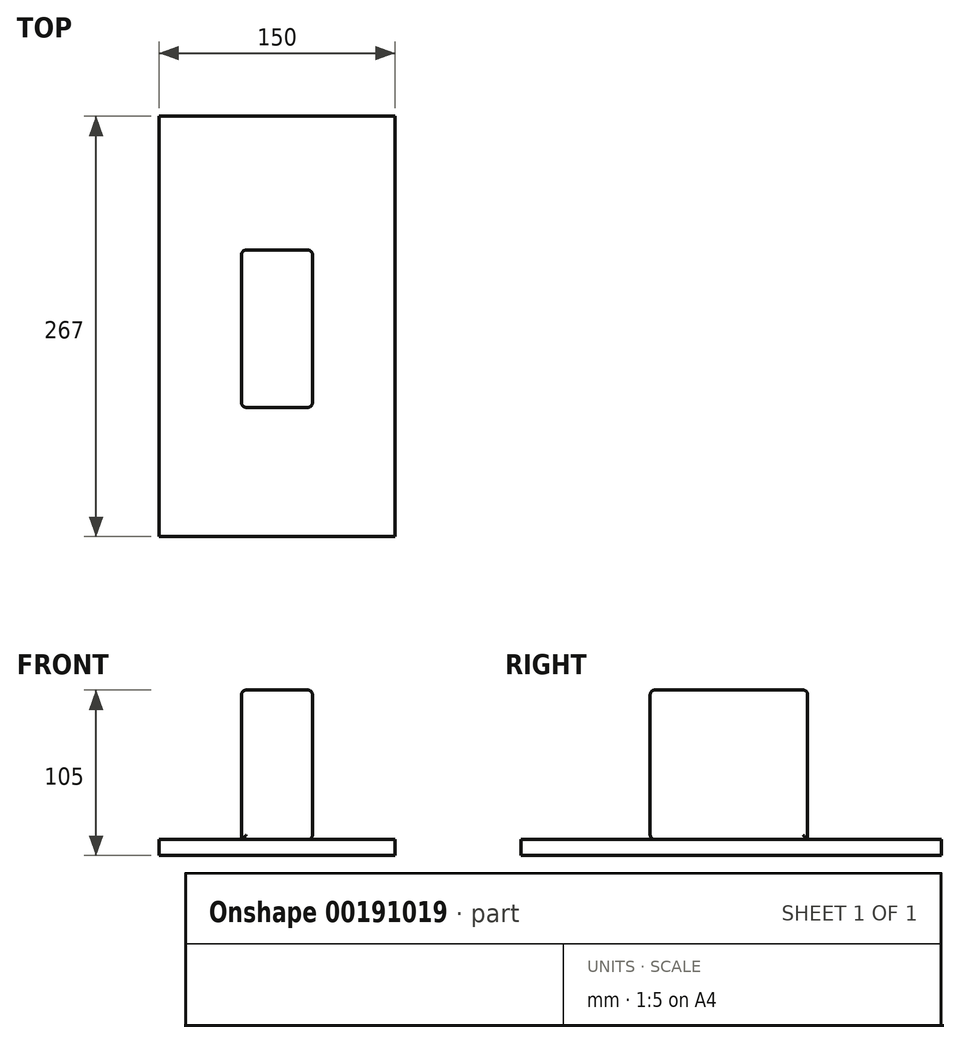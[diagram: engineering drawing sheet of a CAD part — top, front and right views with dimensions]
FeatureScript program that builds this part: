
annotation { "Feature Type Name" : "Feature", "Feature Type Description" : "" }
export const myFeature = defineFeature(function(context is Context, id is Id, definition is map)
    precondition{}
    {
        {
            var Q0;
            Q0=qCreatedBy(makeId("Front.planeOp"),FACE);
            var sketch = newSketch(context, id + "F0", { "sketchPlane" : qUnion([Q0])});
            skLineSegment(sketch, "E0.bottom", {"start": v(-22.5, -47.5) * mm, "end": v(22.5, -47.5) * mm});
            skLineSegment(sketch, "E0.top", {"start": v(-22.5, 47.5) * mm, "end": v(22.5, 47.5) * mm});
            skLineSegment(sketch, "E0.left", {"start": v(-22.5, -47.5) * mm, "end": v(-22.5, 47.5) * mm});
            skLineSegment(sketch, "E0.right", {"start": v(22.5, -47.5) * mm, "end": v(22.5, 47.5) * mm});
            skPoint(sketch, "E0.middle", {"position": v(0, 0) * mm});
            skSolve(sketch);
        }
        {
            var Q0;
            Q0 = qSketchRegion(id + "F0", true);
            extrude(context, id + "F1", {"entities" : qUnion([Q0]), "depth" : 100 * mm});
        }
        {
            var Q0;
            Q0=makeQuery(id+"F1.opExtrude","CAP_EDGE",EDGE,{"disambiguationData":[OSD([sQuery(id+"F0.wireOp",EDGE,"E0.right")])],"isStart":false});
            var Q1;
            Q1=makeQuery(id+"F1.opExtrude","CAP_FACE",FACE,{"disambiguationData":[OSD([sQuery(id+"F0.wireOp",EDGE,"E0.bottom"),sQuery(id+"F0.wireOp",EDGE,"E0.top"),sQuery(id+"F0.wireOp",EDGE,"E0.left"),sQuery(id+"F0.wireOp",EDGE,"E0.right")])],"isStart":false});
            var Q2;
            Q2=makeQuery(id+"F1.opExtrude","CAP_EDGE",EDGE,{"disambiguationData":[OSD([sQuery(id+"F0.wireOp",EDGE,"E0.right")])],"isStart":true});
            var Q3;
            Q3=makeQuery(id+"F1.opExtrude","CAP_EDGE",EDGE,{"disambiguationData":[OSD([sQuery(id+"F0.wireOp",EDGE,"E0.left")])],"isStart":true});
            var Q4;
            Q4=makeQuery(id+"F1.opExtrude","SWEPT_FACE",FACE,{"disambiguationData":[OSD([sQuery(id+"F0.wireOp",EDGE,"E0.right")])]});
            var Q5;
            Q5=makeQuery(id+"F1.opExtrude","SWEPT_EDGE",EDGE,{"disambiguationData":[OSD([sQuery(id+"F0.wireOp",EDGE,"E0.top"),sQuery(id+"F0.wireOp",EDGE,"E0.left")])]});
            var Q6;
            Q6=makeQuery(id+"F1.opExtrude","CAP_EDGE",EDGE,{"disambiguationData":[OSD([sQuery(id+"F0.wireOp",EDGE,"E0.top")])],"isStart":true});
            fillet(context, id + "F2", {"entities" : qUnion([Q0, Q1, Q2, Q3, Q4, Q5, Q6]), "radius" : 3 * mm, "tangentPropagation" : true, "allowEdgeOverflow" : false});
        }
        {
            var Q0;
            Q0=makeQuery(id+"F1.opExtrude","SWEPT_FACE",FACE,{"disambiguationData":[OSD([sQuery(id+"F0.wireOp",EDGE,"E0.bottom")])]});
            var sketch = newSketch(context, id + "F3", { "sketchPlane" : qUnion([Q0])});
            skLineSegment(sketch, "E1.0.0", {"start": v(-22.5, 97) * mm, "end": v(-22.5, 3) * mm, "construction": true});
            skArc(sketch, "E1.0.1", {"start": v(-22.5, 3) * mm, "mid": v(-21.62, 0.88) * mm, "end": v(-19.5, 0) * mm, "construction": true});
            skLineSegment(sketch, "E1.0.2", {"start": v(-19.5, 0) * mm, "end": v(19.5, 0) * mm, "construction": true});
            skLineSegment(sketch, "E1.0.3", {"start": v(19.5, 0) * mm, "end": v(19.5, 97) * mm, "construction": true});
            skLineSegment(sketch, "E1.0.4", {"start": v(19.5, 97) * mm, "end": v(-22.5, 97) * mm, "construction": true});
            skLineSegment(sketch, "E2.bottom", {"start": v(-75, 182) * mm, "end": v(75, 182) * mm});
            skLineSegment(sketch, "E2.top", {"start": v(-75, -85) * mm, "end": v(75, -85) * mm});
            skLineSegment(sketch, "E2.left", {"start": v(-75, 182) * mm, "end": v(-75, -85) * mm});
            skLineSegment(sketch, "E2.right", {"start": v(75, 182) * mm, "end": v(75, -85) * mm});
            skPoint(sketch, "E2.middle", {"position": v(0, 48.5) * mm});
            skPoint(sketch, "E2.middle.positionSnap0", {"position": v(19.5, 48.5) * mm});
            skPoint(sketch, "E2.centerSnap0", {"position": v(19.5, 48.5) * mm});
            skSolve(sketch);
        }
        {
            var Q0;
            Q0 = qSketchRegion(id + "F3", true);
            extrude(context, id + "F4", {"entities" : qUnion([Q0]), "depth" : 10 * mm});
        }
    });
